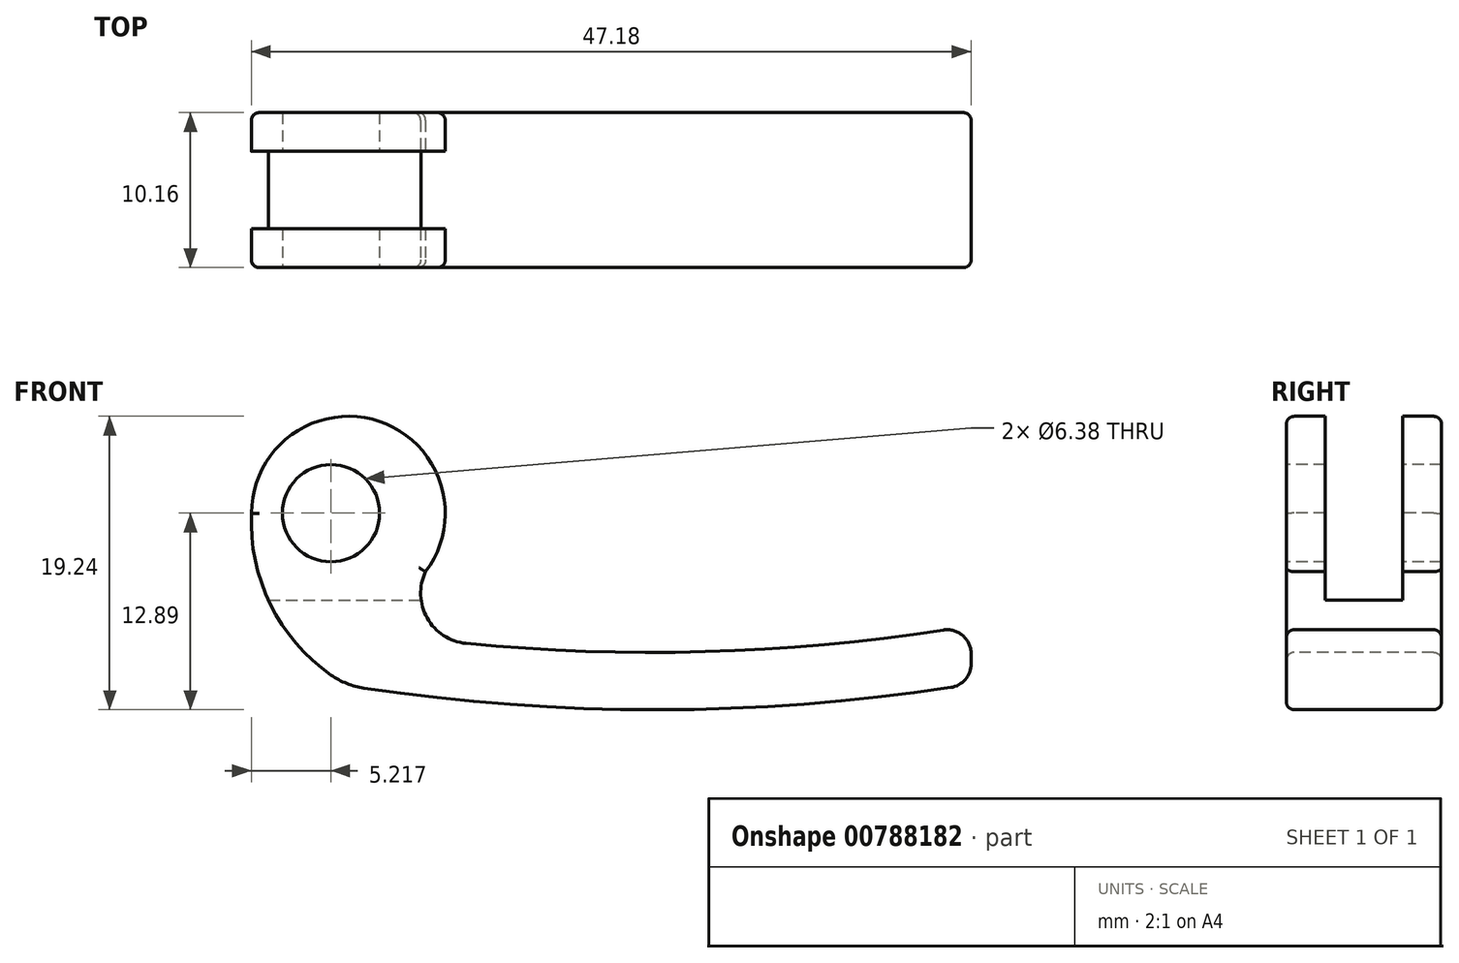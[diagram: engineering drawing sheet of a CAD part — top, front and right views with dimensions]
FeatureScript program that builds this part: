
annotation { "Feature Type Name" : "Feature", "Feature Type Description" : "" }
export const myFeature = defineFeature(function(context is Context, id is Id, definition is map)
    precondition{}
    {
        {
            var Q0;
            Q0=qCreatedBy(makeId("Front.planeOp"),FACE);
            var sketch = newSketch(context, id + "F0", { "sketchPlane" : qUnion([Q0])});
            skArc(sketch, "E0", {"start": v(5.06, -3.84) * mm, "mid": v(2.02, 6.02) * mm, "end": v(-6.35, 0) * mm});
            skCircle(sketch, "E1", {"center": v(-1.14, 0) * mm, "radius": 3.19 * mm});
            skArc(sketch, "E2", {"start": v(0, -11.31) * mm, "mid": v(20.42, -12.89) * mm, "end": v(40.82, -11.22) * mm});
            skLineSegment(sketch, "E3", {"start": v(40.82, -11.22) * mm, "end": v(40.82, -7.36) * mm});
            skArc(sketch, "E4", {"start": v(-6.35, 0) * mm, "mid": v(-4.8, -6.57) * mm, "end": v(0, -11.31) * mm});
            skPoint(sketch, "E5.end.orphan", {"position": v(-7.62, -12.7) * mm});
            skArc(sketch, "E6.trimOffspring", {"start": v(7.71, -8.54) * mm, "mid": v(24.3, -9.05) * mm, "end": v(40.82, -7.36) * mm});
            skArc(sketch, "E7", {"start": v(5.06, -3.84) * mm, "mid": v(5.17, -6.88) * mm, "end": v(7.71, -8.54) * mm});
            skSolve(sketch);
        }
        {
            var Q0;
            Q0=qSketchRegion(id+"F0",true);
            extrude(context, id + "F1", {"entities" : qUnion([Q0]), "oppositeDirection" : true, "depth" : 10.16 * mm});
        }
        {
            var Q0;
            Q0=makeQuery(id+"F1.opExtrude","SWEPT_EDGE",EDGE,{"disambiguationData":[OSD([sQuery(id+"F0.wireOp",EDGE,"E3"),sQuery(id+"F0.wireOp",EDGE,"E6.trimOffspring")])]});
            var Q1;
            Q1=makeQuery(id+"F1.opExtrude","SWEPT_EDGE",EDGE,{"disambiguationData":[OSD([sQuery(id+"F0.wireOp",EDGE,"E2"),sQuery(id+"F0.wireOp",EDGE,"E3")])]});
            fillet(context, id + "F2", {"entities" : qUnion([Q0, Q1]), "radius" : 1.57 * mm, "tangentPropagation" : true, "allowEdgeOverflow" : false});
        }
        {
            var Q0;
            Q0=makeQuery(id+"F1.opExtrude","SWEPT_EDGE",EDGE,{"disambiguationData":[OSD([sQuery(id+"F0.wireOp",EDGE,"E2"),sQuery(id+"F0.wireOp",EDGE,"E4")])]});
            fillet(context, id + "F3", {"entities" : qUnion([Q0]), "radius" : 5.08 * mm, "tangentPropagation" : true, "allowEdgeOverflow" : false});
        }
        {
            var Q0;
            Q0=qCreatedBy(makeId("Right.planeOp"),FACE);
            var sketch = newSketch(context, id + "F4", { "sketchPlane" : qUnion([Q0])});
            skLineSegment(sketch, "E8.bottom", {"start": v(2.54, 7.62) * mm, "end": v(7.62, 7.62) * mm});
            skLineSegment(sketch, "E8.top", {"start": v(2.54, -5.72) * mm, "end": v(7.62, -5.72) * mm});
            skLineSegment(sketch, "E8.left", {"start": v(2.54, 7.62) * mm, "end": v(2.54, -5.72) * mm});
            skLineSegment(sketch, "E8.right", {"start": v(7.62, 7.62) * mm, "end": v(7.62, -5.72) * mm});
            skSolve(sketch);
        }
        {
            var Q0;
            Q0=qSketchRegion(id+"F4",true);
            extrude(context, id + "F5", {"entities" : qUnion([Q0]), "operationType" : NewBodyOperationType.REMOVE, "endBound" : BoundingType.SYMMETRIC, "oppositeDirection" : true, "depth" : 25.4 * mm});
        }
        {
            var Q0;
            Q0=makeQuery(id+"F1.opExtrude","CAP_EDGE",EDGE,{"disambiguationData":[OSD([sQuery(id+"F0.wireOp",EDGE,"E0")])],"isStart":true});
            var Q1;
            Q1=makeQuery(id+"F1.opExtrude","CAP_EDGE",EDGE,{"disambiguationData":[OSD([sQuery(id+"F0.wireOp",EDGE,"0e883233-1986-4913-ab26-c8f9ff4e69e5")])],"isStart":true});
            var Q2;
            Q2=makeQuery(id+"F1.opExtrude","CAP_EDGE",EDGE,{"disambiguationData":[OSD([sQuery(id+"F0.wireOp",EDGE,"E6.trimOffspring")])],"isStart":true});
            var Q3;
            {var subQ0=sQuery(id+"F0.wireOp",EDGE,"E3");var subQ1=sQuery(id+"F0.wireOp",EDGE,"E6.trimOffspring");Q3=makeQuery(id+"F2.opFillet","BLEND_EDGE",EDGE,{"blendedFrom":[makeQuery(id+"F1.opExtrude","SWEPT_EDGE",EDGE,{"disambiguationData":[OSD([subQ0,subQ1])]}),makeQuery(id+"F1.opExtrude","CAP_FACE",FACE,{"disambiguationData":[OSD([sQuery(id+"F0.wireOp",EDGE,"E0"),sQuery(id+"F0.wireOp",EDGE,"E1"),sQuery(id+"F0.wireOp",EDGE,"E2"),sQuery(id+"F0.wireOp",EDGE,"0e883233-1986-4913-ab26-c8f9ff4e69e5"),subQ0,sQuery(id+"F0.wireOp",EDGE,"E4"),subQ1])],"isStart":true})],"blendedInto":[makeQuery(id+"F1.opExtrude","CAP_FACE",FACE,{"disambiguationData":[OSD([sQuery(id+"F0.wireOp",EDGE,"E0"),sQuery(id+"F0.wireOp",EDGE,"E1"),sQuery(id+"F0.wireOp",EDGE,"E2"),sQuery(id+"F0.wireOp",EDGE,"0e883233-1986-4913-ab26-c8f9ff4e69e5"),subQ0,sQuery(id+"F0.wireOp",EDGE,"E4"),subQ1])],"isStart":true})]});}
            var Q4;
            Q4=makeQuery(id+"F1.opExtrude","CAP_EDGE",EDGE,{"disambiguationData":[OSD([sQuery(id+"F0.wireOp",EDGE,"E3")])],"isStart":true});
            var Q5;
            {var subQ0=sQuery(id+"F0.wireOp",EDGE,"E2");var subQ1=sQuery(id+"F0.wireOp",EDGE,"E3");Q5=makeQuery(id+"F2.opFillet","BLEND_EDGE",EDGE,{"blendedFrom":[makeQuery(id+"F1.opExtrude","SWEPT_EDGE",EDGE,{"disambiguationData":[OSD([subQ0,subQ1])]}),makeQuery(id+"F1.opExtrude","CAP_FACE",FACE,{"disambiguationData":[OSD([sQuery(id+"F0.wireOp",EDGE,"E0"),sQuery(id+"F0.wireOp",EDGE,"E1"),subQ0,sQuery(id+"F0.wireOp",EDGE,"0e883233-1986-4913-ab26-c8f9ff4e69e5"),subQ1,sQuery(id+"F0.wireOp",EDGE,"E4"),sQuery(id+"F0.wireOp",EDGE,"E6.trimOffspring")])],"isStart":true})],"blendedInto":[makeQuery(id+"F1.opExtrude","CAP_FACE",FACE,{"disambiguationData":[OSD([sQuery(id+"F0.wireOp",EDGE,"E0"),sQuery(id+"F0.wireOp",EDGE,"E1"),subQ0,sQuery(id+"F0.wireOp",EDGE,"0e883233-1986-4913-ab26-c8f9ff4e69e5"),subQ1,sQuery(id+"F0.wireOp",EDGE,"E4"),sQuery(id+"F0.wireOp",EDGE,"E6.trimOffspring")])],"isStart":true})]});}
            var Q6;
            Q6=makeQuery(id+"F1.opExtrude","CAP_EDGE",EDGE,{"disambiguationData":[OSD([sQuery(id+"F0.wireOp",EDGE,"E2")])],"isStart":true});
            var Q7;
            {var subQ0=sQuery(id+"F0.wireOp",EDGE,"E2");var subQ1=sQuery(id+"F0.wireOp",EDGE,"E4");Q7=makeQuery(id+"F3.opFillet","BLEND_EDGE",EDGE,{"blendedFrom":[makeQuery(id+"F1.opExtrude","SWEPT_EDGE",EDGE,{"disambiguationData":[OSD([subQ0,subQ1])]}),makeQuery(id+"F1.opExtrude","CAP_FACE",FACE,{"disambiguationData":[OSD([sQuery(id+"F0.wireOp",EDGE,"E0"),sQuery(id+"F0.wireOp",EDGE,"E1"),subQ0,sQuery(id+"F0.wireOp",EDGE,"0e883233-1986-4913-ab26-c8f9ff4e69e5"),sQuery(id+"F0.wireOp",EDGE,"E3"),subQ1,sQuery(id+"F0.wireOp",EDGE,"E6.trimOffspring")])],"isStart":true})],"blendedInto":[makeQuery(id+"F1.opExtrude","CAP_FACE",FACE,{"disambiguationData":[OSD([sQuery(id+"F0.wireOp",EDGE,"E0"),sQuery(id+"F0.wireOp",EDGE,"E1"),subQ0,sQuery(id+"F0.wireOp",EDGE,"0e883233-1986-4913-ab26-c8f9ff4e69e5"),sQuery(id+"F0.wireOp",EDGE,"E3"),subQ1,sQuery(id+"F0.wireOp",EDGE,"E6.trimOffspring")])],"isStart":true})]});}
            var Q8;
            Q8=makeQuery(id+"F1.opExtrude","CAP_EDGE",EDGE,{"disambiguationData":[OSD([sQuery(id+"F0.wireOp",EDGE,"E4")])],"isStart":true});
            var Q9;
            Q9=makeQuery(id+"F1.opExtrude","CAP_EDGE",EDGE,{"disambiguationData":[OSD([sQuery(id+"F0.wireOp",EDGE,"E2")])],"isStart":false});
            var Q10;
            {var subQ0=sQuery(id+"F0.wireOp",EDGE,"E2");var subQ1=sQuery(id+"F0.wireOp",EDGE,"E3");Q10=makeQuery(id+"F2.opFillet","BLEND_EDGE",EDGE,{"blendedFrom":[makeQuery(id+"F1.opExtrude","SWEPT_EDGE",EDGE,{"disambiguationData":[OSD([subQ0,subQ1])]}),makeQuery(id+"F1.opExtrude","CAP_FACE",FACE,{"disambiguationData":[OSD([sQuery(id+"F0.wireOp",EDGE,"E0"),sQuery(id+"F0.wireOp",EDGE,"E1"),subQ0,sQuery(id+"F0.wireOp",EDGE,"0e883233-1986-4913-ab26-c8f9ff4e69e5"),subQ1,sQuery(id+"F0.wireOp",EDGE,"E4"),sQuery(id+"F0.wireOp",EDGE,"E6.trimOffspring")])],"isStart":false})],"blendedInto":[makeQuery(id+"F1.opExtrude","CAP_FACE",FACE,{"disambiguationData":[OSD([sQuery(id+"F0.wireOp",EDGE,"E0"),sQuery(id+"F0.wireOp",EDGE,"E1"),subQ0,sQuery(id+"F0.wireOp",EDGE,"0e883233-1986-4913-ab26-c8f9ff4e69e5"),subQ1,sQuery(id+"F0.wireOp",EDGE,"E4"),sQuery(id+"F0.wireOp",EDGE,"E6.trimOffspring")])],"isStart":false})]});}
            var Q11;
            Q11=makeQuery(id+"F1.opExtrude","CAP_EDGE",EDGE,{"disambiguationData":[OSD([sQuery(id+"F0.wireOp",EDGE,"E3")])],"isStart":false});
            var Q12;
            {var subQ0=sQuery(id+"F0.wireOp",EDGE,"E3");var subQ1=sQuery(id+"F0.wireOp",EDGE,"E6.trimOffspring");Q12=makeQuery(id+"F2.opFillet","BLEND_EDGE",EDGE,{"blendedFrom":[makeQuery(id+"F1.opExtrude","SWEPT_EDGE",EDGE,{"disambiguationData":[OSD([subQ0,subQ1])]}),makeQuery(id+"F1.opExtrude","CAP_FACE",FACE,{"disambiguationData":[OSD([sQuery(id+"F0.wireOp",EDGE,"E0"),sQuery(id+"F0.wireOp",EDGE,"E1"),sQuery(id+"F0.wireOp",EDGE,"E2"),sQuery(id+"F0.wireOp",EDGE,"0e883233-1986-4913-ab26-c8f9ff4e69e5"),subQ0,sQuery(id+"F0.wireOp",EDGE,"E4"),subQ1])],"isStart":false})],"blendedInto":[makeQuery(id+"F1.opExtrude","CAP_FACE",FACE,{"disambiguationData":[OSD([sQuery(id+"F0.wireOp",EDGE,"E0"),sQuery(id+"F0.wireOp",EDGE,"E1"),sQuery(id+"F0.wireOp",EDGE,"E2"),sQuery(id+"F0.wireOp",EDGE,"0e883233-1986-4913-ab26-c8f9ff4e69e5"),subQ0,sQuery(id+"F0.wireOp",EDGE,"E4"),subQ1])],"isStart":false})]});}
            var Q13;
            Q13=makeQuery(id+"F1.opExtrude","CAP_EDGE",EDGE,{"disambiguationData":[OSD([sQuery(id+"F0.wireOp",EDGE,"E6.trimOffspring")])],"isStart":false});
            var Q14;
            Q14=makeQuery(id+"F1.opExtrude","CAP_EDGE",EDGE,{"disambiguationData":[OSD([sQuery(id+"F0.wireOp",EDGE,"0e883233-1986-4913-ab26-c8f9ff4e69e5")])],"isStart":false});
            var Q15;
            Q15=makeQuery(id+"F1.opExtrude","CAP_EDGE",EDGE,{"disambiguationData":[OSD([sQuery(id+"F0.wireOp",EDGE,"E0")])],"isStart":false});
            var Q16;
            Q16=makeQuery(id+"F1.opExtrude","CAP_EDGE",EDGE,{"disambiguationData":[OSD([sQuery(id+"F0.wireOp",EDGE,"E4")])],"isStart":false});
            var Q17;
            {var subQ0=sQuery(id+"F0.wireOp",EDGE,"E2");var subQ1=sQuery(id+"F0.wireOp",EDGE,"E4");Q17=makeQuery(id+"F3.opFillet","BLEND_EDGE",EDGE,{"blendedFrom":[makeQuery(id+"F1.opExtrude","SWEPT_EDGE",EDGE,{"disambiguationData":[OSD([subQ0,subQ1])]}),makeQuery(id+"F1.opExtrude","CAP_FACE",FACE,{"disambiguationData":[OSD([sQuery(id+"F0.wireOp",EDGE,"E0"),sQuery(id+"F0.wireOp",EDGE,"E1"),subQ0,sQuery(id+"F0.wireOp",EDGE,"0e883233-1986-4913-ab26-c8f9ff4e69e5"),sQuery(id+"F0.wireOp",EDGE,"E3"),subQ1,sQuery(id+"F0.wireOp",EDGE,"E6.trimOffspring")])],"isStart":false})],"blendedInto":[makeQuery(id+"F1.opExtrude","CAP_FACE",FACE,{"disambiguationData":[OSD([sQuery(id+"F0.wireOp",EDGE,"E0"),sQuery(id+"F0.wireOp",EDGE,"E1"),subQ0,sQuery(id+"F0.wireOp",EDGE,"0e883233-1986-4913-ab26-c8f9ff4e69e5"),sQuery(id+"F0.wireOp",EDGE,"E3"),subQ1,sQuery(id+"F0.wireOp",EDGE,"E6.trimOffspring")])],"isStart":false})]});}
            fillet(context, id + "F6", {"entities" : qUnion([Q0, Q1, Q2, Q3, Q4, Q5, Q6, Q7, Q8, Q9, Q10, Q11, Q12, Q13, Q14, Q15, Q16, Q17]), "radius" : 0.5 * mm, "tangentPropagation" : true, "allowEdgeOverflow" : false});
        }
    });
